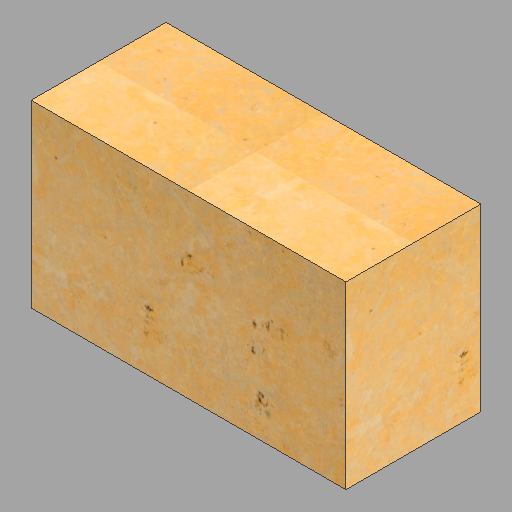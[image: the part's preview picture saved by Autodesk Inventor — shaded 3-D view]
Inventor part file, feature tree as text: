
AUTODESK INVENTOR PART (.ipt)
format: ipt  version: 2023 (Build 270158030, 158C)  size: 400,896 bytes
history: native  units: in
note: dims shown in document units (in); Inventor stores cm internally (conversion verified against a paired STEP export)
features: other x1, extrude x1, sketch x1
ambient origin geometry x8: Origin, YZ Plane, XZ Plane, XY Plane, X Axis, Y Axis, Z Axis, Center Point
bodies: Solid1 (feature_tree)
feature tree (3):
  other  "Bench typ2 - 4"
  extrude  "Extrusion1"  Depth=18.0in
  sketch  "Sketch1"  dims[d0=42.0in d1=18.0in d2=24.0in d3=0.0in]
